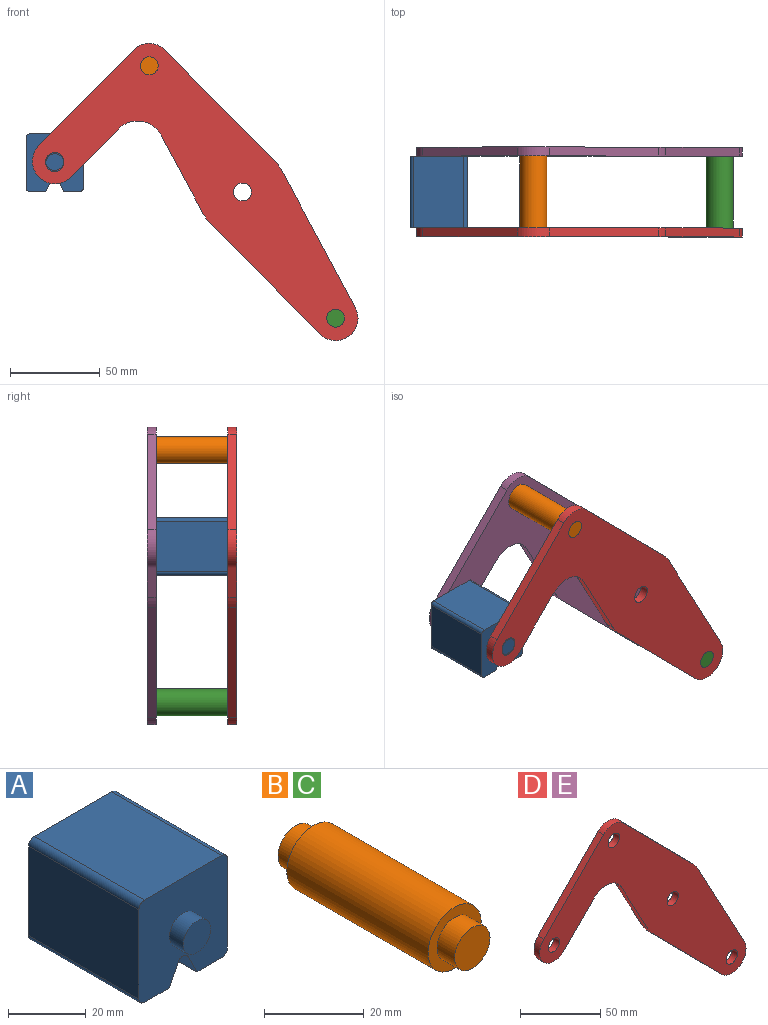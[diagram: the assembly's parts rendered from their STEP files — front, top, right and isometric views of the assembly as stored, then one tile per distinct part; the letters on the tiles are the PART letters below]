
ASSEMBLY  parts=5 mates=3
PART A: 18 faces, bbox 32.1x50x32.1 mm
  f0: plane 40x28.08mm, normal (1,0,0), area 1123.1mm2, adj f4,f10,f13,f14
  f1: plane 40x9.04mm, normal (0,0,-1), area 361.6mm2, adj f2,f4,f10,f14
  f2: plane 40x6.42mm, normal (-0.89,0,-0.45), area 287.2mm2, adj f1,f4,f10,f15
  f3: plane 40x6.42mm, normal (0.89,0,-0.45), area 287.2mm2, adj f4,f5,f10,f15
  f4: plane 32.08x32.08mm, normal (0,-1,0), area 900.6mm2, adj f0,f1,f2,f3,f5,f6,f7,f9
  f5: plane 40x9.04mm, normal (0,0,-1), area 361.6mm2, adj f3,f4,f10,f16
  f6: plane 40x28.08mm, normal (0,0,1), area 1123.1mm2, adj f4,f10,f13,f17
  f7: plane 40x28.08mm, normal (-1,0,0), area 1123.1mm2, adj f4,f10,f16,f17
  f8: plane 10x10mm, normal (0,-1,0), area 78.5mm2, adj f9
  f9: cylinder r=5mm len=10mm, axis (0,1,0), area 157.1mm2, adj f4,f8
  f10: plane 32.08x32.08mm, normal (0,1,0), area 900.6mm2, adj f0,f1,f2,f3,f5,f6,f7,f12
  f11: plane 10x10mm, normal (0,1,0), area 78.5mm2, adj f12
  f12: cylinder r=5mm len=10mm, axis (0,-1,0), area 157.1mm2, adj f10,f11
  f13: cylinder r=2mm len=40mm, axis (0,1,0), area 125.7mm2, adj f0,f4,f6,f10
  f14: cylinder r=2mm len=40mm, axis (0,-1,0), area 125.7mm2, adj f0,f1,f4,f10
  f15: cylinder r=2mm len=40mm, axis (0,1,0), area 177.1mm2, adj f2,f3,f4,f10
  f16: cylinder r=2mm len=40mm, axis (0,1,0), area 125.7mm2, adj f4,f5,f7,f10
  f17: cylinder r=2mm len=40mm, axis (0,-1,0), area 125.7mm2, adj f4,f6,f7,f10
PART B: 7 faces, bbox 15x50x15 mm
  f0: cylinder r=7.5mm len=40mm, axis (0,-1,0), area 1885mm2, adj f2,f5
  f1: cylinder r=5mm len=10mm, axis (0,1,0), area 157.1mm2, adj f2,f3
  f2: plane 15x15mm, normal (0,-1,0), area 98.2mm2, adj f0,f1
  f3: plane 10x10mm, normal (0,-1,0), area 78.5mm2, adj f1
  f4: cylinder r=5mm len=10mm, axis (0,-1,0), area 157.1mm2, adj f5,f6
  f5: plane 15x15mm, normal (0,1,0), area 98.2mm2, adj f0,f4
  f6: plane 10x10mm, normal (0,1,0), area 78.5mm2, adj f4
PART C: same geometry as B
PART D: 18 faces, bbox 181.7x5x165.8 mm
  f0: plane 43.49x23.35mm, normal (-0.88,0,-0.47), area 246.8mm2, adj f1,f14,f16,f17
  f1: cylinder r=25mm len=5.75mm, axis (0,1,0), area 35.8mm2, adj f0,f2,f16,f17
  f2: plane 61.6x60.87mm, normal (-0.71,0,-0.7), area 433mm2, adj f1,f3,f16,f17
  f3: cylinder r=12.5mm len=21.39mm, axis (0,1,0), area 178.4mm2, adj f2,f4,f16,f17
  f4: plane 76.3x40.96mm, normal (0.88,0,0.47), area 433mm2, adj f3,f5,f16,f17
  f5: cylinder r=25mm len=5.75mm, axis (0,1,0), area 35.8mm2, adj f4,f6,f16,f17
  f6: plane 61.6x60.87mm, normal (0.71,0,0.7), area 433mm2, adj f5,f7,f16,f17
  f7: cylinder r=12.5mm len=17.78mm, axis (0,1,0), area 98.9mm2, adj f6,f8,f16,f17
  f8: plane 53.35x52.71mm, normal (-0.71,0,0.7), area 375mm2, adj f7,f9,f16,f17
  f9: cylinder r=12.5mm len=21.39mm, axis (0,1,0), area 196.3mm2, adj f8,f10,f16,f17
  f10: plane 26.86x26.54mm, normal (0.71,0,-0.7), area 188.8mm2, adj f9,f14,f16,f17
  f11: cylinder r=5mm len=10mm, axis (0,1,0), area 157.1mm2, adj f16,f17
  f12: cylinder r=5mm len=10mm, axis (0,1,0), area 157.1mm2, adj f16,f17
  f13: cylinder r=5mm len=10mm, axis (0,1,0), area 157.1mm2, adj f16,f17
  f14: cylinder r=15mm len=23.89mm, axis (0,1,0), area 140.2mm2, adj f0,f10,f16,f17
  f15: cylinder r=5mm len=10mm, axis (0,1,0), area 157.1mm2, adj f16,f17
  f16: plane 181.66x165.78mm, normal (0,-1,0), area 8710.1mm2, adj f0,f1,f2,f3,f4,f5,f6,f7
  f17: plane 181.66x165.78mm, normal (0,1,0), area 8710.1mm2, adj f0,f1,f2,f3,f4,f5,f6,f7
PART E: same geometry as D
PLACE A t=(0,0,-0.67)mm
PLACE B at identity
PLACE C t=(103.95,0,-140.78)mm
PLACE D at identity fixed
PLACE E t=(0,45,0)mm
MATE fastened E.f7 <-> B.f0  axis (0,-1,0) through (-51.98,40,70.39)mm
MATE fastened C.f0 <-> D.f3  axis (0,-1,0) through (51.98,0,-70.39)mm
MATE revolute D.f9 <-> A.f4  axis (0,1,0) through (-104.69,0,17.04)mm
